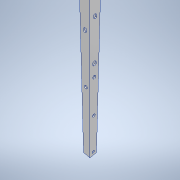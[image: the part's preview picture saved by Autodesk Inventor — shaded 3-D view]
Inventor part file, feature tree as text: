
AUTODESK INVENTOR PART (.ipt)
format: ipt  version: 2020.3 (Build 243373000, 373)  size: 146,432 bytes
history: native  units: mm
features: sketch x5, hole x4, other x1, extrude x1
ambient origin geometry x8: Origin, YZ Plane, XZ Plane, XY Plane, X Axis, Y Axis, Z Axis, Center Point
bodies: Body1 (feature_tree)
feature tree (11):
  other  "ソリッド1"
  extrude  "押し出し1"  Depth=9.0mm
  hole  "穴1"  [1 undecoded]
  hole  "穴2"  [1 undecoded]
  hole  "穴3"  [1 undecoded]
  hole  "穴4"  [1 undecoded]
  sketch  "スケッチ1"
  sketch  "スケッチ2"
  sketch  "スケッチ3"
  sketch  "スケッチ4"
  sketch  "スケッチ5"
note: 4 required parameter values undecoded (feature->parameter linkage not recoverable at this tier; creation-order binding heuristic only, values carry confidence <= 0.55)
